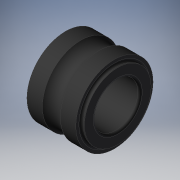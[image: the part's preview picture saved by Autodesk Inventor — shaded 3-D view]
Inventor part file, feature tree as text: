
AUTODESK INVENTOR PART (.ipt)
format: ipt  version: 2019 (Build 230136000, 136)  size: 204,288 bytes
history: native  units: mm
features: revolve x2, sketch x2
ambient origin geometry x8: Origin, YZ Plane, XZ Plane, XY Plane, X Axis, Y Axis, Z Axis, Center Point
bodies: Solid1 (feature_tree)
feature tree (4):
  revolve  "Revolution1"  Angle=360.0deg
  revolve  "Revolution2"  [1 undecoded]
  sketch  "Sketch_40"  dims[d0=360.0deg d1=360.0deg]
  sketch  "Sketch_42"
note: 1 required parameter value undecoded (feature->parameter linkage not recoverable at this tier; creation-order binding heuristic only, values carry confidence <= 0.55)
